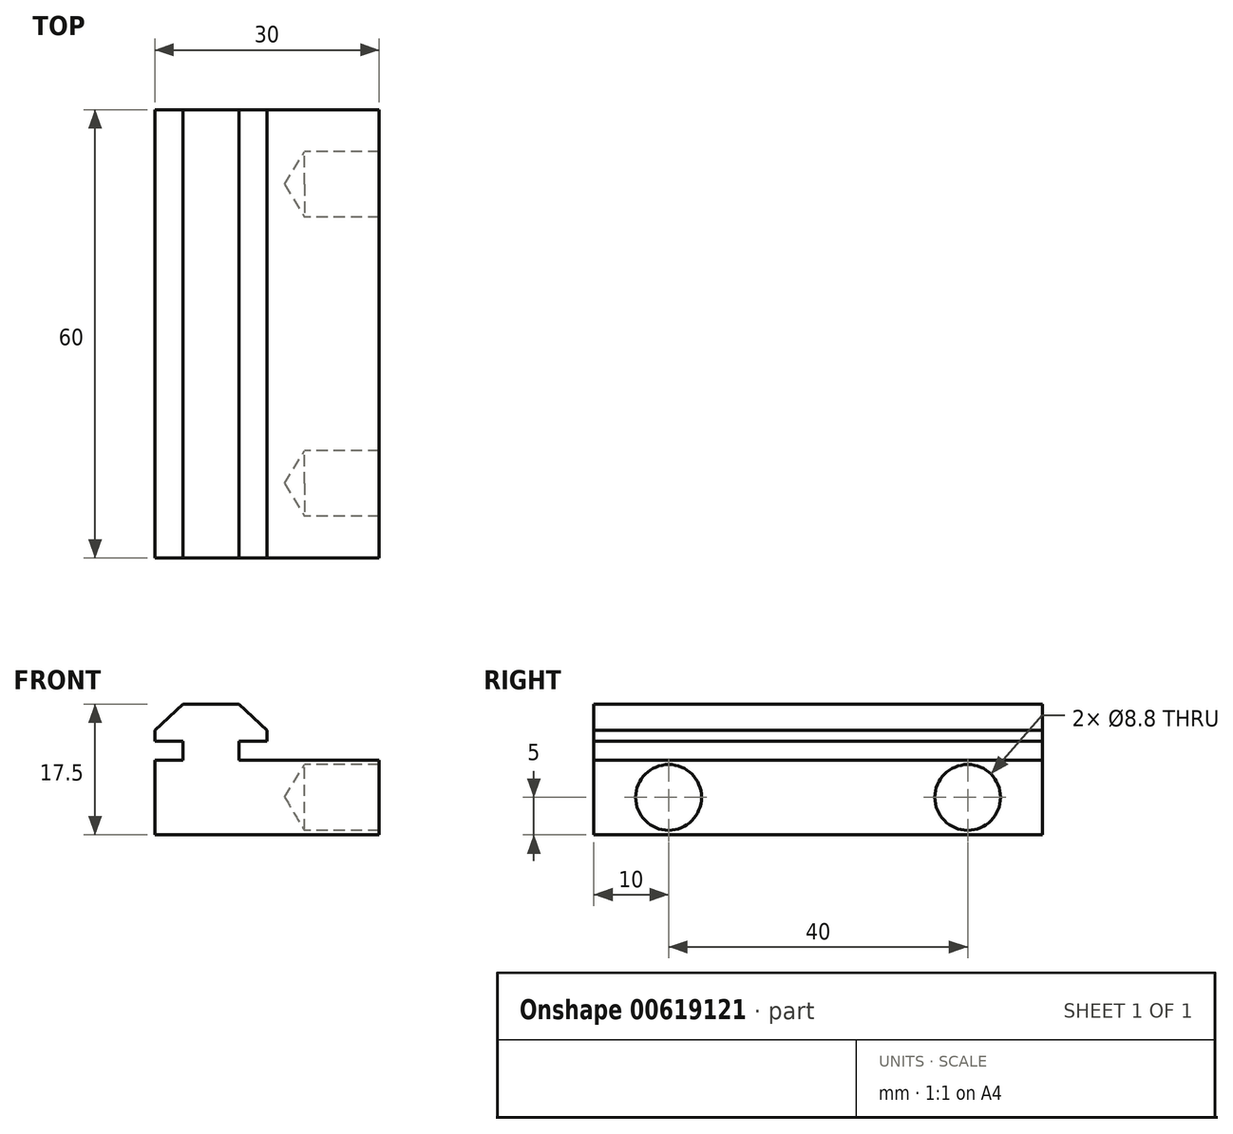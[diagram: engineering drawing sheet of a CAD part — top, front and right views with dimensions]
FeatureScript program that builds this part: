
annotation { "Feature Type Name" : "Feature", "Feature Type Description" : "" }
export const myFeature = defineFeature(function(context is Context, id is Id, definition is map)
    precondition{}
    {
        {
            var Q0;
            Q0=qCreatedBy(makeId("Front.planeOp"),FACE);
            var sketch = newSketch(context, id + "F0", { "sketchPlane" : qUnion([Q0])});
            skLineSegment(sketch, "E0", {"start": v(-3.77, 0) * mm, "end": v(-3.77, 2.5) * mm});
            skLineSegment(sketch, "E1", {"start": v(-3.77, 2.5) * mm, "end": v(-7.52, 2.5) * mm});
            skLineSegment(sketch, "E2", {"start": v(-7.52, 2.5) * mm, "end": v(-7.52, 4) * mm});
            skLineSegment(sketch, "E3", {"start": v(-7.52, 4) * mm, "end": v(-3.77, 7.5) * mm});
            skLineSegment(sketch, "E4", {"start": v(-3.77, 7.5) * mm, "end": v(3.73, 7.5) * mm});
            skLineSegment(sketch, "E5", {"start": v(3.73, 7.5) * mm, "end": v(7.48, 4) * mm});
            skLineSegment(sketch, "E6", {"start": v(7.48, 4) * mm, "end": v(7.48, 2.5) * mm});
            skLineSegment(sketch, "E7", {"start": v(7.48, 2.5) * mm, "end": v(3.73, 2.5) * mm});
            skLineSegment(sketch, "E8", {"start": v(3.73, 2.5) * mm, "end": v(3.73, 0) * mm});
            skLineSegment(sketch, "E9", {"start": v(3.73, 0) * mm, "end": v(-3.77, 0) * mm});
            skLineSegment(sketch, "E10.bottom", {"start": v(-7.52, 0) * mm, "end": v(22.48, 0) * mm});
            skLineSegment(sketch, "E10.top", {"start": v(-7.52, -10) * mm, "end": v(22.48, -10) * mm});
            skLineSegment(sketch, "E10.left", {"start": v(-7.52, 0) * mm, "end": v(-7.52, -10) * mm});
            skLineSegment(sketch, "E10.right", {"start": v(22.48, 0) * mm, "end": v(22.48, -10) * mm});
            skSolve(sketch);
        }
        {
            var Q0;
            Q0=qSketchRegion(id+"F0",true);
            extrude(context, id + "F1", {"entities" : qUnion([Q0]), "depth" : 60 * mm, "offsetDistance" : 25 * mm});
        }
        {
            var Q0;
            Q0=makeQuery(id+"F1.opExtrude","SWEPT_FACE",FACE,{"disambiguationData":[OSD([sQuery(id+"F0.wireOp",EDGE,"E10.right")])]});
            var sketch = newSketch(context, id + "F2", { "sketchPlane" : qUnion([Q0])});
            skPoint(sketch, "E11", {"position": v(-50, -5) * mm});
            skPoint(sketch, "E11.positionSnap0", {"position": v(-60, -5) * mm});
            skPoint(sketch, "E12", {"position": v(-10, -5) * mm});
            skSolve(sketch);
        }
        {
            var Q0;
            Q0=sQuery(id+"F2.wireOp",VERTEX,"E11");
            var Q1;
            Q1=sQuery(id+"F2.wireOp",VERTEX,"E12");
            var Q2;
            Q2=makeQuery(id+"F1.opExtrude","SWEPT_BODY",BODY,{"disambiguationData":[OSD([sQuery(id+"F0.wireOp",EDGE,"E0"),sQuery(id+"F0.wireOp",EDGE,"E1"),sQuery(id+"F0.wireOp",EDGE,"E2"),sQuery(id+"F0.wireOp",EDGE,"E3"),sQuery(id+"F0.wireOp",EDGE,"E4"),sQuery(id+"F0.wireOp",EDGE,"E5"),sQuery(id+"F0.wireOp",EDGE,"E6"),sQuery(id+"F0.wireOp",EDGE,"E7"),sQuery(id+"F0.wireOp",EDGE,"E8"),sQuery(id+"F0.wireOp",EDGE,"E10.bottom"),sQuery(id+"F0.wireOp",EDGE,"E10.top"),sQuery(id+"F0.wireOp",EDGE,"E10.left"),sQuery(id+"F0.wireOp",EDGE,"E10.right")])]});
            hole(context, id + "F3", {"style" : HoleStyle.SIMPLE, "endStyle" : HoleEndStyle.BLIND, "standardTappedOrClearance" : lookupTablePath({ "standard" : "ISO", "fit" : "Normal", "size" : "M8", "type" : "Clearance" }), "standardBlindInLast" : lookupTablePath({ "fit" : "Standard", "standard" : "ISO", "size" : "M8", "type" : "Clearance" }), "holeDiameter" : 8.8 * mm, "majorDiameter" : 5 * mm, "holeDepth" : 10 * mm, "isTappedThrough" : true, "tappedDepth" : 12 * mm, "tapClearance" : 3, "locations" : qUnion([Q0, Q1]), "scope" : qUnion([Q2]), "startStyle" : HoleStartStyle.SKETCH});
        }
    });
